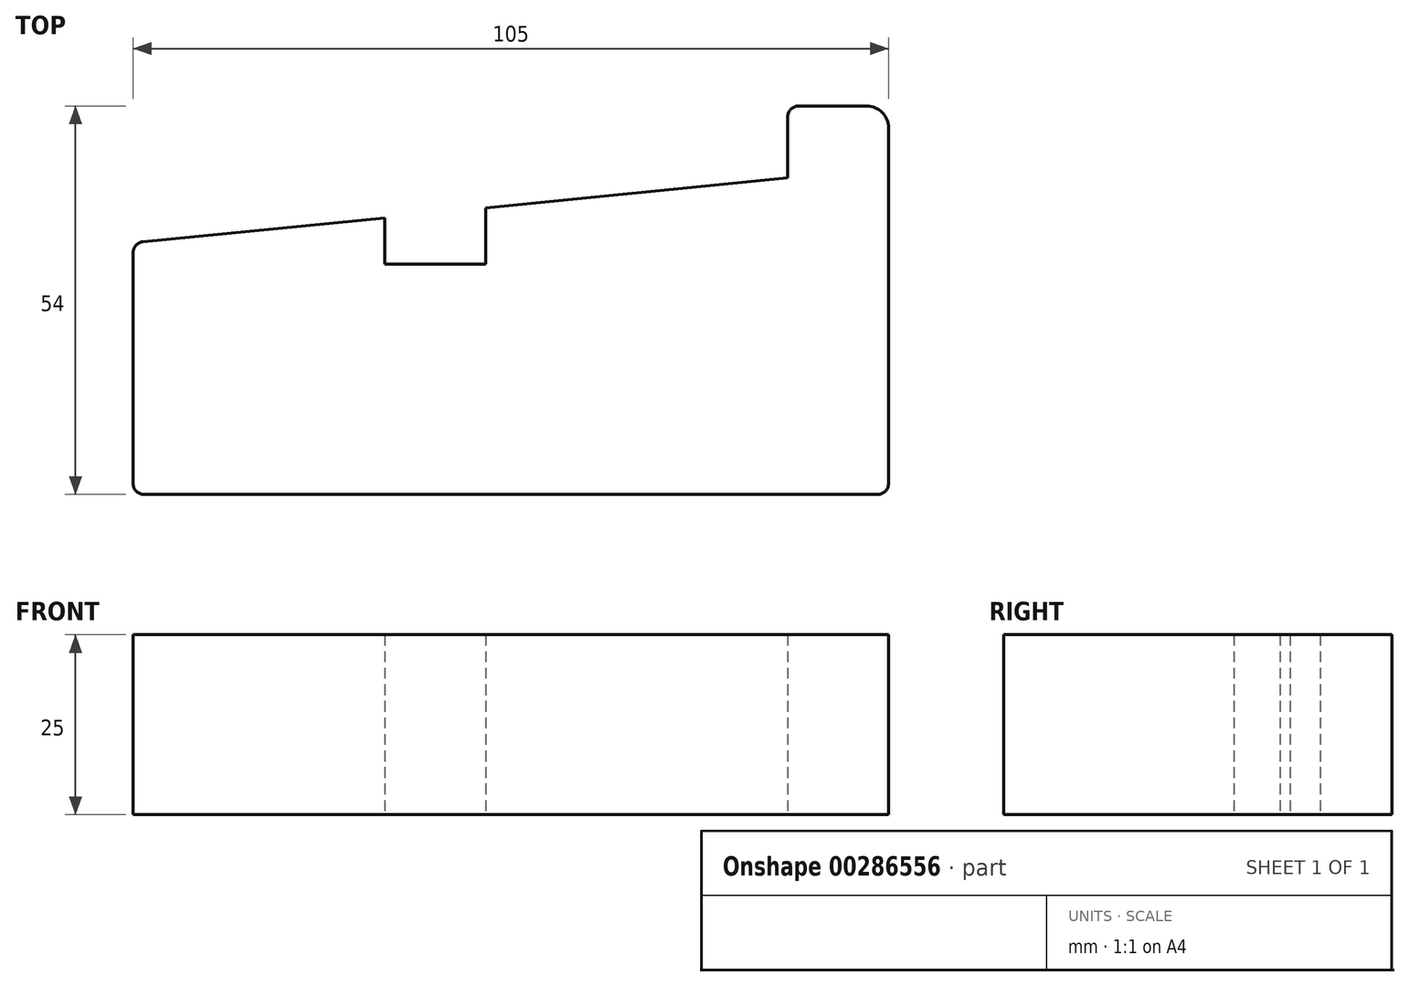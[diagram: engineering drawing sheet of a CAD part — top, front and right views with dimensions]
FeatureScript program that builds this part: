
annotation { "Feature Type Name" : "Feature", "Feature Type Description" : "" }
export const myFeature = defineFeature(function(context is Context, id is Id, definition is map)
    precondition{}
    {
        {
            var Q0;
            Q0=qCreatedBy(makeId("Top.planeOp"),FACE);
            var sketch = newSketch(context, id + "F0", { "sketchPlane" : qUnion([Q0])});
            skLineSegment(sketch, "E0", {"start": v(-16.77, -44) * mm, "end": v(37.73, -44) * mm});
            skLineSegment(sketch, "E1", {"start": v(39.23, -42.5) * mm, "end": v(39.23, 7) * mm});
            skLineSegment(sketch, "E2", {"start": v(36.23, 10) * mm, "end": v(26.73, 10) * mm});
            skLineSegment(sketch, "E3", {"start": v(25.23, 8.5) * mm, "end": v(25.23, 0) * mm});
            skPoint(sketch, "E4.start.orphan", {"position": v(-9.77, -37.92) * mm});
            skPoint(sketch, "E5.start.orphan", {"position": v(-9.77, -48.64) * mm});
            skPoint(sketch, "E6.visualSharp", {"position": v(39.23, 10) * mm});
            skArc(sketch, "E6.filletArc", {"start": v(39.23, 7) * mm, "mid": v(38.36, 9.12) * mm, "end": v(36.23, 10) * mm});
            skPoint(sketch, "E7.visualSharp", {"position": v(39.23, -44) * mm});
            skArc(sketch, "E7.filletArc", {"start": v(37.73, -44) * mm, "mid": v(38.8, -43.56) * mm, "end": v(39.23, -42.5) * mm});
            skPoint(sketch, "E8.visualSharp", {"position": v(-65.77, -9) * mm});
            skPoint(sketch, "E9.visualSharp", {"position": v(-65.77, -44) * mm});
            skPoint(sketch, "E10.visualSharp", {"position": v(25.23, 10) * mm});
            skArc(sketch, "E10.filletArc", {"start": v(26.73, 10) * mm, "mid": v(25.67, 9.56) * mm, "end": v(25.23, 8.5) * mm});
            skPoint(sketch, "E11.start.orphan", {"position": v(-9.77, -12) * mm});
            skLineSegment(sketch, "E12", {"start": v(-16.77, -47.35) * mm, "end": v(-16.77, -44) * mm});
            skLineSegment(sketch, "E13", {"start": v(-16.77, -12) * mm, "end": v(-30.77, -12) * mm});
            skLineSegment(sketch, "E14", {"start": v(-16.77, -4.15) * mm, "end": v(25.23, 0) * mm});
            skLineSegment(sketch, "E15", {"start": v(-30.77, -12) * mm, "end": v(-30.77, -5.54) * mm});
            skLineSegment(sketch, "E16", {"start": v(-16.77, -12) * mm, "end": v(-16.77, -4.15) * mm});
            skLineSegment(sketch, "E17", {"start": v(-30.77, -5.54) * mm, "end": v(-64.41, -8.87) * mm});
            skLineSegment(sketch, "E18", {"start": v(-16.77, -44) * mm, "end": v(-64.27, -44) * mm});
            skLineSegment(sketch, "E19", {"start": v(-65.77, -10.36) * mm, "end": v(-65.77, -42.5) * mm});
            skArc(sketch, "E20.filletArc", {"start": v(-64.41, -8.87) * mm, "mid": v(-65.38, -9.35) * mm, "end": v(-65.77, -10.36) * mm});
            skArc(sketch, "E21.filletArc", {"start": v(-65.77, -42.5) * mm, "mid": v(-65.33, -43.56) * mm, "end": v(-64.27, -44) * mm});
            skSolve(sketch);
        }
        {
            var Q0;
            Q0 = qSketchRegion(id + "F0", true);
            extrude(context, id + "F1", {"entities" : qUnion([Q0]), "depth" : 25 * mm});
        }
    });
